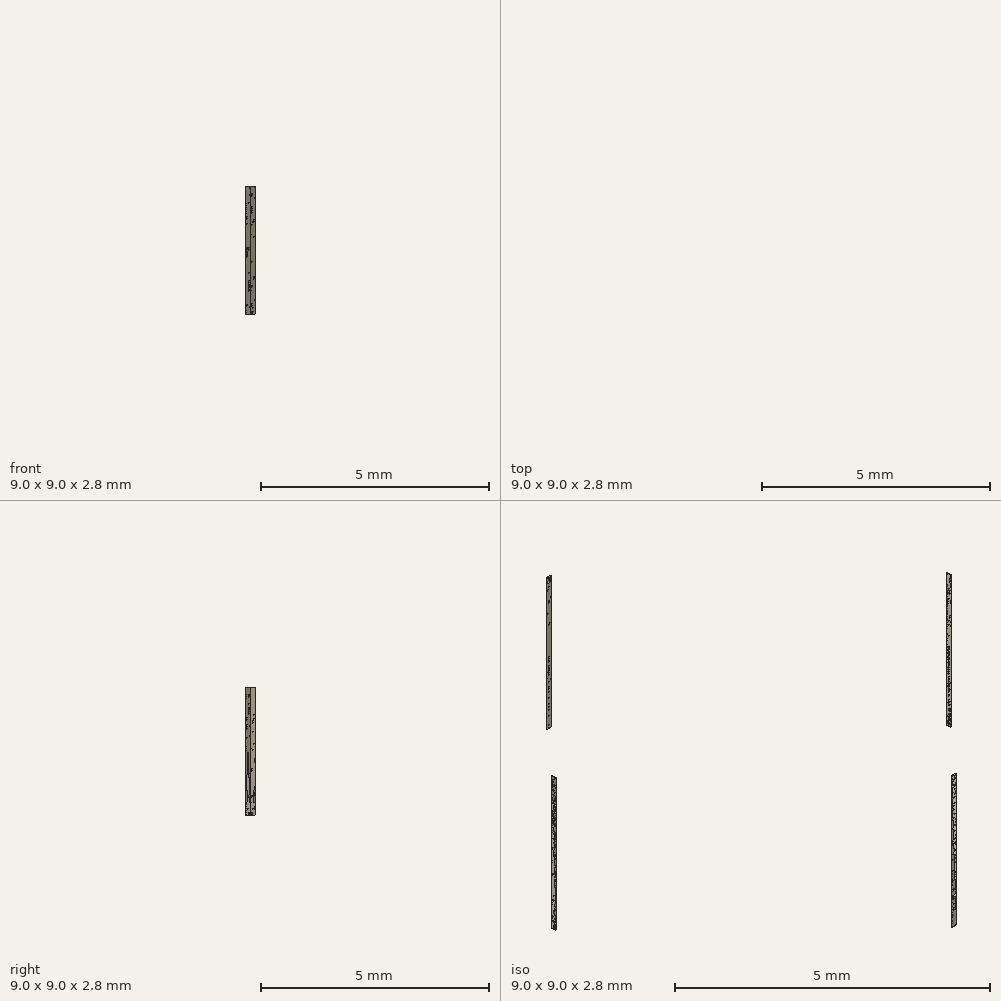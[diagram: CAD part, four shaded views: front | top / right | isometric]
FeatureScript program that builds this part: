
annotation { "Feature Type Name" : "Feature", "Feature Type Description" : "" }
export const myFeature = defineFeature(function(context is Context, id is Id, definition is map)
    precondition{}
    {
        {
            var Q0;
            Q0=qCreatedBy(makeId("Top.planeOp"),FACE);
            var sketch = newSketch(context, id + "F0", { "sketchPlane" : qUnion([Q0])});
            skCircle(sketch, "E0", {"center": v(0, 0) * mm, "radius": 11 * mm});
            skSolve(sketch);
        }
        {
            var Q0;
            Q0=makeQuery(id+"F0.imprint","IMPRINT",FACE,{"disambiguationData":[TD([[makeQuery(id+"F0.imprint","IMPRINT",EDGE,{"derivedFrom":sQuery(id+"F0.wireOp",EDGE,"E0")}),1.0]])]});
            extrude(context, id + "F1", {"entities" : qUnion([Q0]), "depth" : 2 * mm, "offsetDistance" : 25 * mm});
        }
        {
            var Q0;
            Q0=makeQuery(id+"F1.opExtrude","CAP_EDGE",EDGE,{"disambiguationData":[OSD([sQuery(id+"F0.wireOp",EDGE,"E0")])],"isStart":true});
            chamfer(context, id + "F2", {"entities" : qUnion([Q0]), "width" : 1 * mm, "tangentPropagation" : true});
        }
        {
            var Q0;
            Q0=makeQuery(id+"F1.opExtrude","CAP_FACE",FACE,{"disambiguationData":[OSD([sQuery(id+"F0.wireOp",EDGE,"E0")])],"isStart":false});
            var sketch = newSketch(context, id + "F3", { "sketchPlane" : qUnion([Q0])});
            skCircle(sketch, "E1", {"center": v(0, 0) * mm, "radius": 6 * mm});
            skSolve(sketch);
        }
        {
            var Q0;
            Q0=makeQuery(id+"F3.imprint","IMPRINT",FACE,{"disambiguationData":[TD([[makeQuery(id+"F3.imprint","IMPRINT",EDGE,{"derivedFrom":sQuery(id+"F3.wireOp",EDGE,"E1")}),1.0]])]});
            extrude(context, id + "F4", {"entities" : qUnion([Q0]), "operationType" : NewBodyOperationType.ADD, "depth" : .2 * mm, "offsetDistance" : 25 * mm});
        }
        {
            var Q0;
            Q0=makeQuery(id+"F4.opExtrude","CAP_FACE",FACE,{"disambiguationData":[OSD([sQuery(id+"F3.wireOp",EDGE,"E1")])],"isStart":false});
            var sketch = newSketch(context, id + "F5", { "sketchPlane" : qUnion([Q0])});
            skCircle(sketch, "E2", {"center": v(0, 0) * mm, "radius": 4.5 * mm});
            skCircle(sketch, "E3", {"center": v(0, 0) * mm, "radius": 2.5 * mm});
            skArc(sketch, "E4", {"start": v(4.5, 0) * mm, "mid": v(3, 2.58) * mm, "end": v(0, 2.5) * mm});
            skArc(sketch, "E5.0", {"start": v(3.7, 0) * mm, "mid": v(2.98, 1.62) * mm, "end": v(1.3, 2.14) * mm});
            skCircle(sketch, "E6.0", {"center": v(0, 0) * mm, "radius": 11 * mm});
            skArc(sketch, "E7", {"start": v(4.5, 0) * mm, "mid": v(4.1, -0.4) * mm, "end": v(3.7, 0) * mm});
            skArc(sketch, "E8.1.0", {"start": v(0, 4.5) * mm, "mid": v(-2.58, 3) * mm, "end": v(-2.5, 0) * mm});
            skArc(sketch, "E8.1.1", {"start": v(0, 3.7) * mm, "mid": v(-1.62, 2.98) * mm, "end": v(-2.14, 1.3) * mm});
            skArc(sketch, "E8.1.2", {"start": v(0, 4.5) * mm, "mid": v(0.4, 4.1) * mm, "end": v(0, 3.7) * mm});
            skArc(sketch, "E8.2.0", {"start": v(-4.5, 0) * mm, "mid": v(-3, -2.58) * mm, "end": v(0, -2.5) * mm});
            skArc(sketch, "E8.2.1", {"start": v(-3.7, 0) * mm, "mid": v(-2.98, -1.62) * mm, "end": v(-1.3, -2.14) * mm});
            skArc(sketch, "E8.2.2", {"start": v(-4.5, 0) * mm, "mid": v(-4.1, 0.4) * mm, "end": v(-3.7, 0) * mm});
            skArc(sketch, "E8.3.0", {"start": v(0, -4.5) * mm, "mid": v(2.58, -3) * mm, "end": v(2.5, 0) * mm});
            skArc(sketch, "E8.3.1", {"start": v(0, -3.7) * mm, "mid": v(1.62, -2.98) * mm, "end": v(2.14, -1.3) * mm});
            skArc(sketch, "E8.3.2", {"start": v(0, -4.5) * mm, "mid": v(-0.4, -4.1) * mm, "end": v(0, -3.7) * mm});
            skSolve(sketch);
        }
        {
            var Q0;
            {var subQ0=sQuery(id+"F5.wireOp",EDGE,"E8.1.0");Q0=makeQuery(id+"F5.imprint","IMPRINT",FACE,{"disambiguationData":[TD([[makeQuery(id+"F5.imprint","IMPRINT",EDGE,{"derivedFrom":subQ0}),1.0]])]});}
            var Q1;
            {var subQ1=sQuery(id+"F5.wireOp",EDGE,"E4");Q1=makeQuery(id+"F5.imprint","IMPRINT",FACE,{"disambiguationData":[TD([[makeQuery(id+"F5.imprint","IMPRINT",EDGE,{"derivedFrom":subQ1}),1.0]])]});}
            var Q2;
            {var subQ1=sQuery(id+"F5.wireOp",EDGE,"E8.3.0");Q2=makeQuery(id+"F5.imprint","IMPRINT",FACE,{"disambiguationData":[TD([[makeQuery(id+"F5.imprint","IMPRINT",EDGE,{"derivedFrom":subQ1}),1.0]])]});}
            var Q3;
            {var subQ0=sQuery(id+"F5.wireOp",EDGE,"E8.2.0");Q3=makeQuery(id+"F5.imprint","IMPRINT",FACE,{"disambiguationData":[TD([[makeQuery(id+"F5.imprint","IMPRINT",EDGE,{"derivedFrom":subQ0}),1.0]])]});}
            var Q4;
            {var subQ0=sQuery(id+"F5.wireOp",EDGE,"E3");var subQ4=makeQuery(id+"F5.imprint","INTERSECT",VERTEX,{"derivedFrom":[subQ0,sQuery(id+"F5.wireOp",EDGE,"E5.0")]});Q4=makeQuery(id+"F5.imprint","IMPRINT",FACE,{"disambiguationData":[TD([[makeQuery(id+"F5.imprint","IMPRINT",EDGE,{"disambiguationData":[TD([[subQ4,1.0]])],"derivedFrom":subQ0}),1.0]])]});}
            extrude(context, id + "F6", {"entities" : qUnion([Q0, Q1, Q2, Q3, Q4]), "operationType" : NewBodyOperationType.ADD, "depth" : 3.2 * mm, "offsetDistance" : 25 * mm});
        }
        {
            var Q0;
            {var subQ0=sQuery(id+"F5.wireOp",EDGE,"E8.2.0");Q0=makeQuery(id+"F5.imprint","IMPRINT",FACE,{"disambiguationData":[TD([[makeQuery(id+"F5.imprint","IMPRINT",EDGE,{"derivedFrom":subQ0}),1.0]])]});}
            var Q1;
            {var subQ0=sQuery(id+"F5.wireOp",EDGE,"E8.1.0");Q1=makeQuery(id+"F5.imprint","IMPRINT",FACE,{"disambiguationData":[TD([[makeQuery(id+"F5.imprint","IMPRINT",EDGE,{"derivedFrom":subQ0}),1.0]])]});}
            var Q2;
            {var subQ1=sQuery(id+"F5.wireOp",EDGE,"E4");Q2=makeQuery(id+"F5.imprint","IMPRINT",FACE,{"disambiguationData":[TD([[makeQuery(id+"F5.imprint","IMPRINT",EDGE,{"derivedFrom":subQ1}),1.0]])]});}
            var Q3;
            {var subQ1=sQuery(id+"F5.wireOp",EDGE,"E8.3.0");Q3=makeQuery(id+"F5.imprint","IMPRINT",FACE,{"disambiguationData":[TD([[makeQuery(id+"F5.imprint","IMPRINT",EDGE,{"derivedFrom":subQ1}),1.0]])]});}
            extrude(context, id + "F7", {"entities" : qUnion([Q0, Q1, Q2, Q3]), "operationType" : NewBodyOperationType.REMOVE, "depth" : .4 * mm, "offsetDistance" : 25 * mm});
        }
    });
